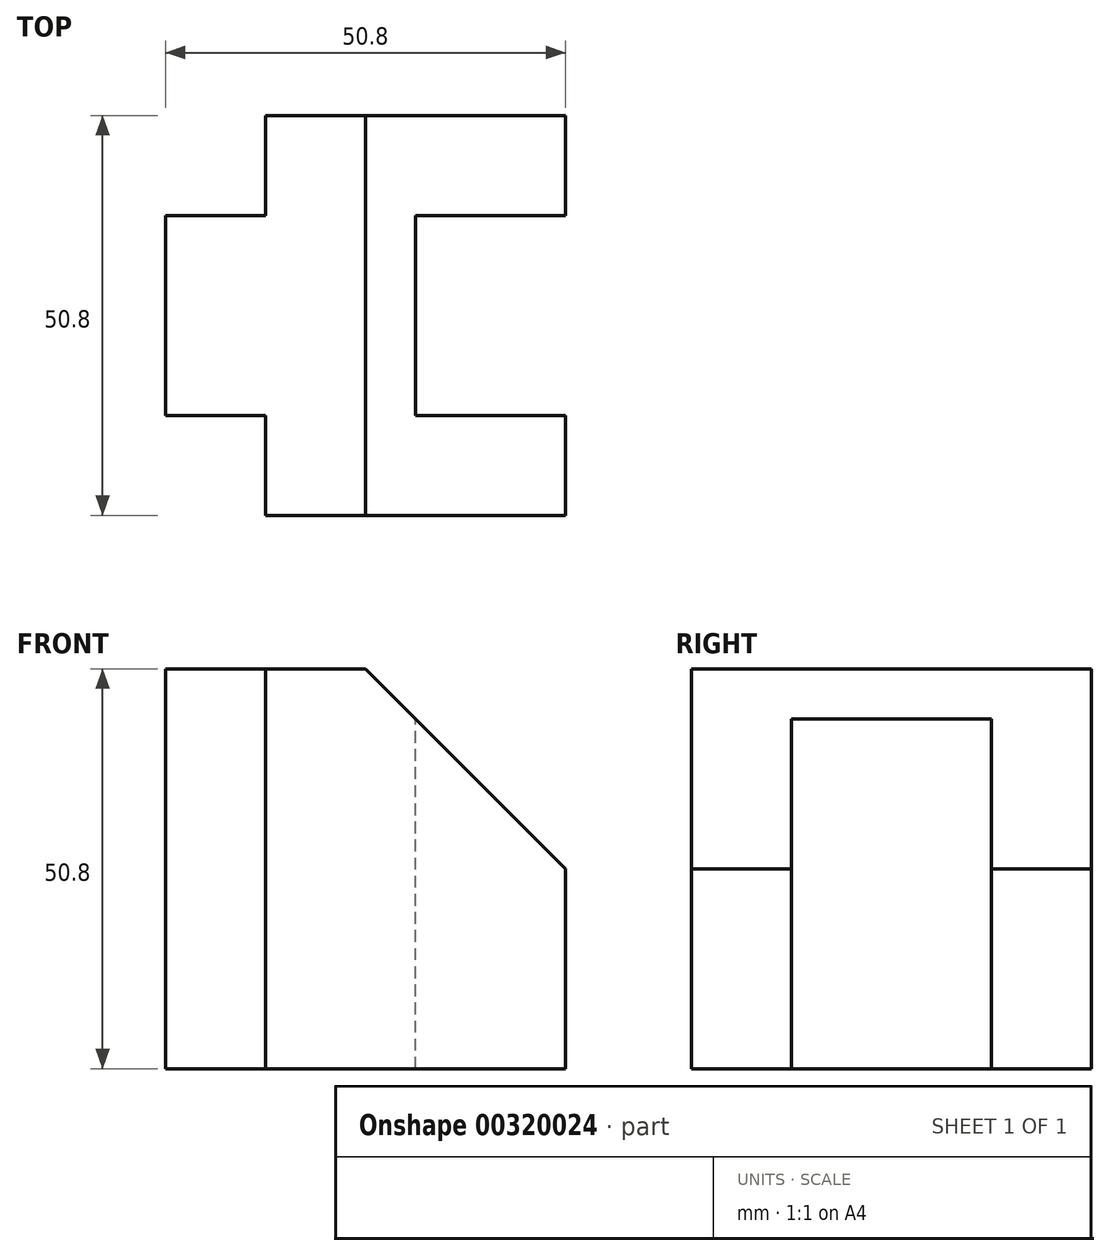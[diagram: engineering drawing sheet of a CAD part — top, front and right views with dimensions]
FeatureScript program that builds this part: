
annotation { "Feature Type Name" : "Feature", "Feature Type Description" : "" }
export const myFeature = defineFeature(function(context is Context, id is Id, definition is map)
    precondition{}
    {
        {
            var Q0;
            Q0=qCreatedBy(makeId("Top.planeOp"),FACE);
            var sketch = newSketch(context, id + "F0", { "sketchPlane" : qUnion([Q0])});
            skLineSegment(sketch, "E0", {"start": v(0, 12.7) * mm, "end": v(12.7, 12.7) * mm});
            skLineSegment(sketch, "E1", {"start": v(12.7, 12.7) * mm, "end": v(12.7, 25.4) * mm});
            skLineSegment(sketch, "E2", {"start": v(12.7, 25.4) * mm, "end": v(50.8, 25.4) * mm});
            skLineSegment(sketch, "E3", {"start": v(50.8, 25.4) * mm, "end": v(50.8, 12.7) * mm});
            skLineSegment(sketch, "E4", {"start": v(50.8, 12.7) * mm, "end": v(31.75, 12.7) * mm});
            skLineSegment(sketch, "E5", {"start": v(31.75, 12.7) * mm, "end": v(31.75, 0) * mm});
            skLineSegment(sketch, "E6", {"start": v(0, 12.7) * mm, "end": v(0, 0) * mm});
            skLineSegment(sketch, "E7", {"start": v(0, 0) * mm, "end": v(88.9, 0) * mm, "construction": true});
            skLineSegment(sketch, "E8.MirrorCS", {"start": v(31.75, -12.7) * mm, "end": v(31.75, 0) * mm});
            skLineSegment(sketch, "E9.MirrorCS", {"start": v(50.8, -12.7) * mm, "end": v(31.75, -12.7) * mm});
            skLineSegment(sketch, "E10.MirrorCS", {"start": v(50.8, -25.4) * mm, "end": v(50.8, -12.7) * mm});
            skLineSegment(sketch, "E11.MirrorCS", {"start": v(12.7, -25.4) * mm, "end": v(50.8, -25.4) * mm});
            skLineSegment(sketch, "E12.MirrorCS", {"start": v(12.7, -12.7) * mm, "end": v(12.7, -25.4) * mm});
            skLineSegment(sketch, "E13.MirrorCS", {"start": v(0, -12.7) * mm, "end": v(12.7, -12.7) * mm});
            skLineSegment(sketch, "E14.MirrorCS", {"start": v(0, -12.7) * mm, "end": v(0, 0) * mm});
            skSolve(sketch);
        }
        {
            var Q0;
            Q0=makeQuery(id+"F0.imprint","IMPRINT",FACE,{"disambiguationData":[TD([[makeQuery(id+"F0.imprint","IMPRINT",EDGE,{"derivedFrom":sQuery(id+"F0.wireOp",EDGE,"E0")}),-1.0]])]});
            extrude(context, id + "F1", {"entities" : qUnion([Q0]), "oppositeDirection" : true, "depth" : 50.8 * mm});
        }
        {
            var Q0;
            Q0=qCreatedBy(makeId("Front.planeOp"),FACE);
            var sketch = newSketch(context, id + "F2", { "sketchPlane" : qUnion([Q0])});
            skLineSegment(sketch, "E15", {"start": v(0, 0) * mm, "end": v(25.4, 0) * mm});
            skLineSegment(sketch, "E16", {"start": v(25.4, 0) * mm, "end": v(50.8, -25.4) * mm});
            skLineSegment(sketch, "E17", {"start": v(50.8, -25.4) * mm, "end": v(50.8, -50.8) * mm});
            skLineSegment(sketch, "E18", {"start": v(50.8, -50.8) * mm, "end": v(0, -50.8) * mm});
            skLineSegment(sketch, "E19", {"start": v(0, -50.8) * mm, "end": v(0, 0) * mm});
            skLineSegment(sketch, "E20", {"start": v(50.8, -25.4) * mm, "end": v(50.8, 0) * mm});
            skLineSegment(sketch, "E21", {"start": v(50.8, 0) * mm, "end": v(25.4, 0) * mm});
            skSolve(sketch);
        }
        {
            var Q0;
            Q0=makeQuery(id+"F2.imprint","IMPRINT",FACE,{"disambiguationData":[TD([[makeQuery(id+"F2.imprint","IMPRINT",EDGE,{"derivedFrom":sQuery(id+"F2.wireOp",EDGE,"E16")}),1.0]])]});
            extrude(context, id + "F3", {"entities" : qUnion([Q0]), "operationType" : NewBodyOperationType.REMOVE, "endBound" : BoundingType.SYMMETRIC, "oppositeDirection" : true, "depth" : 50.8 * mm});
        }
    });
